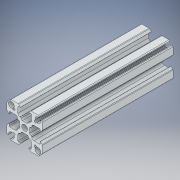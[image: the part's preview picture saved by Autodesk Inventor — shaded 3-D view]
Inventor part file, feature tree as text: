
AUTODESK INVENTOR PART (.ipt)
format: ipt  version: 2017 (Build 210142000, 142)  size: 308,224 bytes
history: native  units: in
note: dims shown in document units (in); Inventor stores cm internally (conversion verified against a paired STEP export)
features: extrude x1, sketch x1, fillet x1
ambient origin geometry x8: Origin, YZ Plane, XZ Plane, XY Plane, X Axis, Y Axis, Z Axis, Center Point
bodies: Solid1 (feature_tree)
feature tree (3):
  extrude  "Extrusion1"  [1 undecoded]
  sketch  "Sketch1"  dims[d0=68.3in d1=0.0in]
  fillet  "Fillet10"  [1 undecoded]
note: 2 required parameter values undecoded (feature->parameter linkage not recoverable at this tier; creation-order binding heuristic only, values carry confidence <= 0.55)
